# Revit family: 221010024038286
name_source: partatom
category: Modelos genéricos
revit_build: Autodesk Revit 2018 (Build: 20190510_1515(x64)
units: mm (PartAtom-declared; Revit-internal decimal feet)

## family parameters
Compartido = No
Corte con vacíos al cargar = No
Cota de conector redondo = Diámetro de uso
Puede alojar armadura = No
Punto de cálculo de habitación = No
Se basa en plano de trabajo = No
Siempre vertical = No
Tipo de pieza = Normal

## types (1)
- LISTON BASE RAINBODECK HPC 50X30MM CAFE TIRA 2.2MT
    Alto = 30 mm  [stored 0.0984252 ft]
    Aplicacion = Base para fijacion de tablas Deck Rainbodeck
    Color = Cafe
    Descripción = Accesorio requerido para la instalación de las tablas de Deck de HPC.
    Dimension = 50 mm  [stored 0.164042 ft]
    Empresa = CNP SPA.
    Espesor = 2 mm  [stored 0.00656168 ft]
    Largo = 2200 mm
    Material = HPC cafe
    Modelo = LISTON BASE RAINBODECK HPC
    Nombre SKU = LISTON BASE RAINBODECK HPC 50X30MM CAFE TIRA 2.2MT
    Num SKUs = 221010024038286
    URL = https://www.empresascnp.cl
    Unidad = Tiras de 2.20 Mts
    Url Ficha tecnica = https://empresascnp.cl

note: [stored X ft] marks values corroborated as IEEE doubles in the binary element streams (Revit-internal decimal feet)

## geometry (parser evidence)
native form markers: Sweep x2
no freeform markers — native parametric forms only
